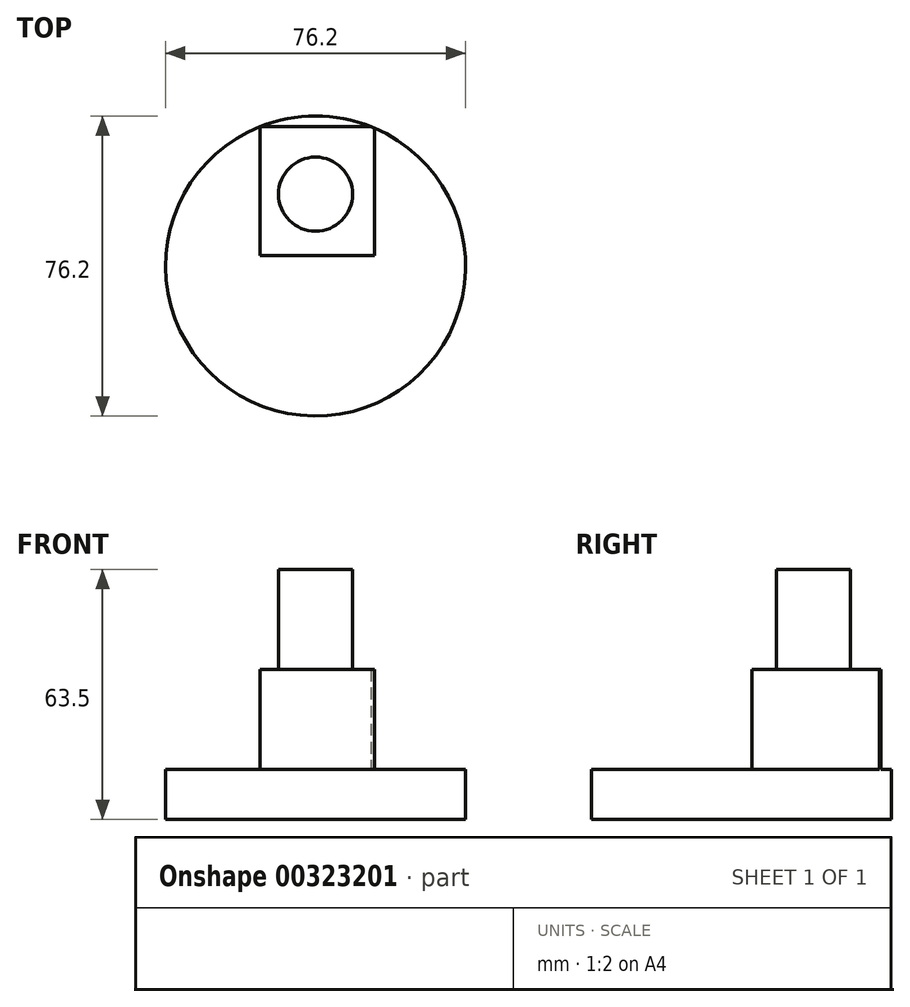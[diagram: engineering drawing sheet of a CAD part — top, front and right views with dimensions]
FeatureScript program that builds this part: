
annotation { "Feature Type Name" : "Feature", "Feature Type Description" : "" }
export const myFeature = defineFeature(function(context is Context, id is Id, definition is map)
    precondition{}
    {
        {
            var Q0;
            Q0=qCreatedBy(makeId("Top.planeOp"),FACE);
            var sketch = newSketch(context, id + "F0", { "sketchPlane" : qUnion([Q0])});
            skCircle(sketch, "E0", {"center": v(0, 0) * mm, "radius": 38.1 * mm});
            skSolve(sketch);
        }
        {
            var Q0;
            Q0=makeQuery(id+"F0.imprint","IMPRINT",FACE,{"disambiguationData":[TD([[makeQuery(id+"F0.imprint","IMPRINT",EDGE,{"derivedFrom":sQuery(id+"F0.wireOp",EDGE,"E0")}),1.0]])]});
            extrude(context, id + "F1", {"entities" : qUnion([Q0]), "depth" : 12.7 * mm});
        }
        {
            var Q0;
            Q0=makeQuery(id+"F1.opExtrude","CAP_FACE",FACE,{"disambiguationData":[OSD([sQuery(id+"F0.wireOp",EDGE,"E0")])],"isStart":false});
            var sketch = newSketch(context, id + "F2", { "sketchPlane" : qUnion([Q0])});
            skLineSegment(sketch, "E1.bottom", {"start": v(-14.1, 35.4) * mm, "end": v(14.92, 35.4) * mm});
            skLineSegment(sketch, "E1.top", {"start": v(-14.1, 2.64) * mm, "end": v(14.92, 2.64) * mm});
            skLineSegment(sketch, "E1.left", {"start": v(-14.1, 35.4) * mm, "end": v(-14.1, 2.64) * mm});
            skLineSegment(sketch, "E1.right", {"start": v(14.92, 35.4) * mm, "end": v(14.92, 2.64) * mm});
            skSolve(sketch);
        }
        {
            var Q0;
            {var subQ1=sQuery(id+"F2.wireOp",EDGE,"E1.top");Q0=makeQuery(id+"F2.imprint","IMPRINT",FACE,{"disambiguationData":[TD([[makeQuery(id+"F2.imprint","IMPRINT",EDGE,{"derivedFrom":subQ1}),1.0]])]});}
            extrude(context, id + "F3", {"entities" : qUnion([Q0]), "operationType" : NewBodyOperationType.ADD, "depth" : 25.4 * mm});
        }
        {
            var Q0;
            Q0=makeQuery(id+"F3.opExtrude","CAP_FACE",FACE,{"disambiguationData":[OSD([sQuery(id+"F0.wireOp",EDGE,"E0"),sQuery(id+"F2.wireOp",EDGE,"E1.bottom"),sQuery(id+"F2.wireOp",EDGE,"E1.top"),sQuery(id+"F2.wireOp",EDGE,"E1.left"),sQuery(id+"F2.wireOp",EDGE,"E1.right")])],"isStart":false});
            var sketch = newSketch(context, id + "F4", { "sketchPlane" : qUnion([Q0])});
            skCircle(sketch, "E2", {"center": v(0, 18.25) * mm, "radius": 9.42 * mm});
            skSolve(sketch);
        }
        {
            var Q0;
            Q0=makeQuery(id+"F4.imprint","IMPRINT",FACE,{"disambiguationData":[TD([[makeQuery(id+"F4.imprint","IMPRINT",EDGE,{"derivedFrom":sQuery(id+"F4.wireOp",EDGE,"E2")}),1.0]])]});
            extrude(context, id + "F5", {"entities" : qUnion([Q0]), "operationType" : NewBodyOperationType.ADD, "depth" : 25.4 * mm});
        }
    });
